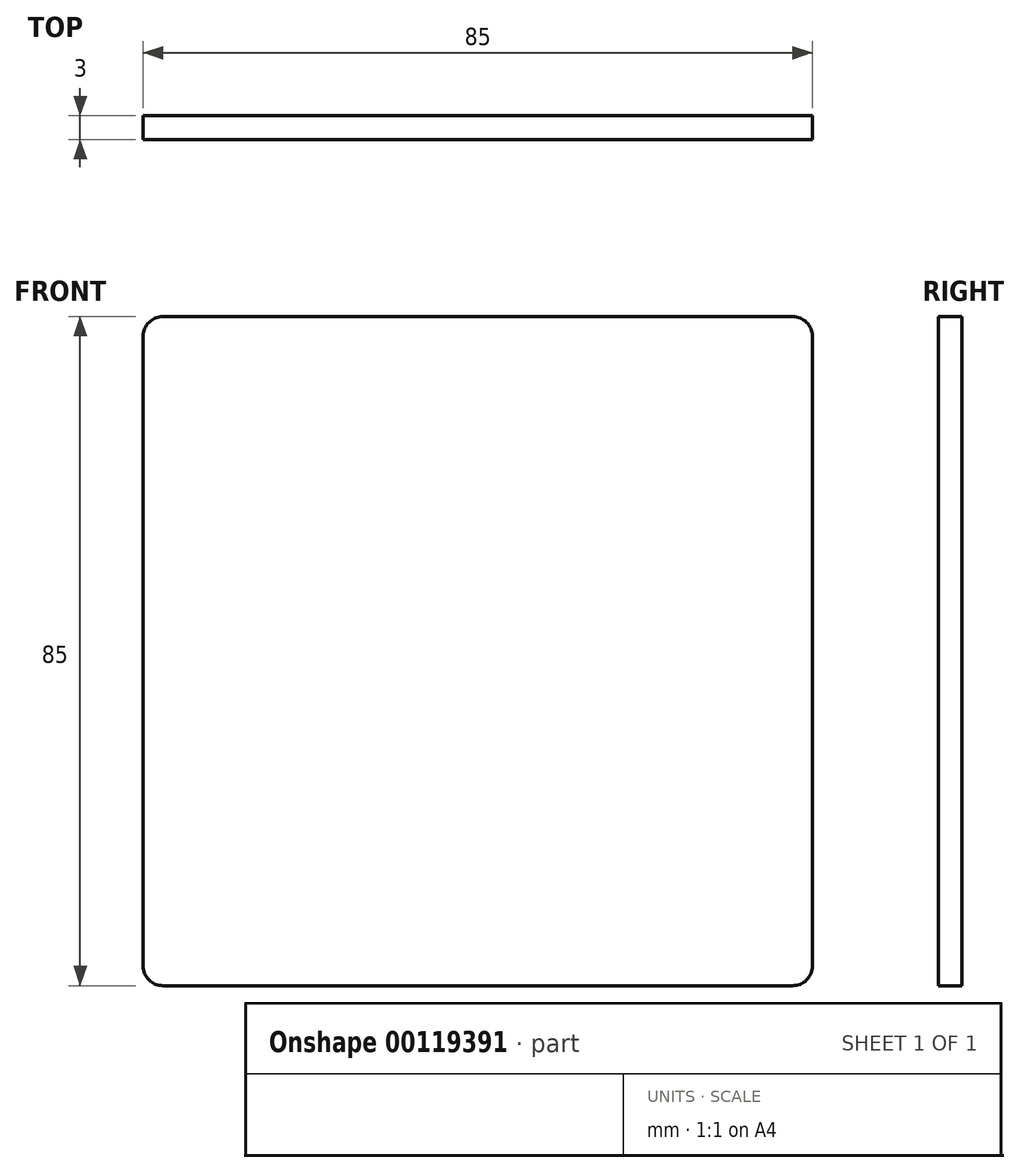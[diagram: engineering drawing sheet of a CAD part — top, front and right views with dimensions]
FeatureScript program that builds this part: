
annotation { "Feature Type Name" : "Feature", "Feature Type Description" : "" }
export const myFeature = defineFeature(function(context is Context, id is Id, definition is map)
    precondition{}
    {
        {
            var Q0;
            Q0=qCreatedBy(makeId("Front.planeOp"),FACE);
            var sketch = newSketch(context, id + "F0", { "sketchPlane" : qUnion([Q0])});
            skLineSegment(sketch, "E0.bottom", {"start": v(40, -42.5) * mm, "end": v(-40, -42.5) * mm});
            skLineSegment(sketch, "E0.top", {"start": v(40, 42.5) * mm, "end": v(-40, 42.5) * mm});
            skLineSegment(sketch, "E0.left", {"start": v(42.5, -40) * mm, "end": v(42.5, 40) * mm});
            skLineSegment(sketch, "E0.right", {"start": v(-42.5, -40) * mm, "end": v(-42.5, 40) * mm});
            skPoint(sketch, "E0.middle", {"position": v(0, 0) * mm});
            skPoint(sketch, "E1.visualSharp", {"position": v(-42.5, 42.5) * mm});
            skArc(sketch, "E1.filletArc", {"start": v(-40, 42.5) * mm, "mid": v(-41.77, 41.77) * mm, "end": v(-42.5, 40) * mm});
            skPoint(sketch, "E2.visualSharp", {"position": v(42.5, 42.5) * mm});
            skArc(sketch, "E2.filletArc", {"start": v(42.5, 40) * mm, "mid": v(41.77, 41.77) * mm, "end": v(40, 42.5) * mm});
            skPoint(sketch, "E3.visualSharp", {"position": v(42.5, -42.5) * mm});
            skArc(sketch, "E3.filletArc", {"start": v(40, -42.5) * mm, "mid": v(41.77, -41.77) * mm, "end": v(42.5, -40) * mm});
            skPoint(sketch, "E4.visualSharp", {"position": v(-42.5, -42.5) * mm});
            skArc(sketch, "E4.filletArc", {"start": v(-42.5, -40) * mm, "mid": v(-41.77, -41.77) * mm, "end": v(-40, -42.5) * mm});
            skSolve(sketch);
        }
        {
            var Q0;
            Q0=makeQuery(id+"F0.imprint","IMPRINT",FACE,{"disambiguationData":[TD([[makeQuery(id+"F0.imprint","IMPRINT",EDGE,{"derivedFrom":sQuery(id+"F0.wireOp",EDGE,"E0.bottom")}),-1.0]])]});
            extrude(context, id + "F1", {"entities" : qUnion([Q0]), "depth" : 3 * mm});
        }
    });
